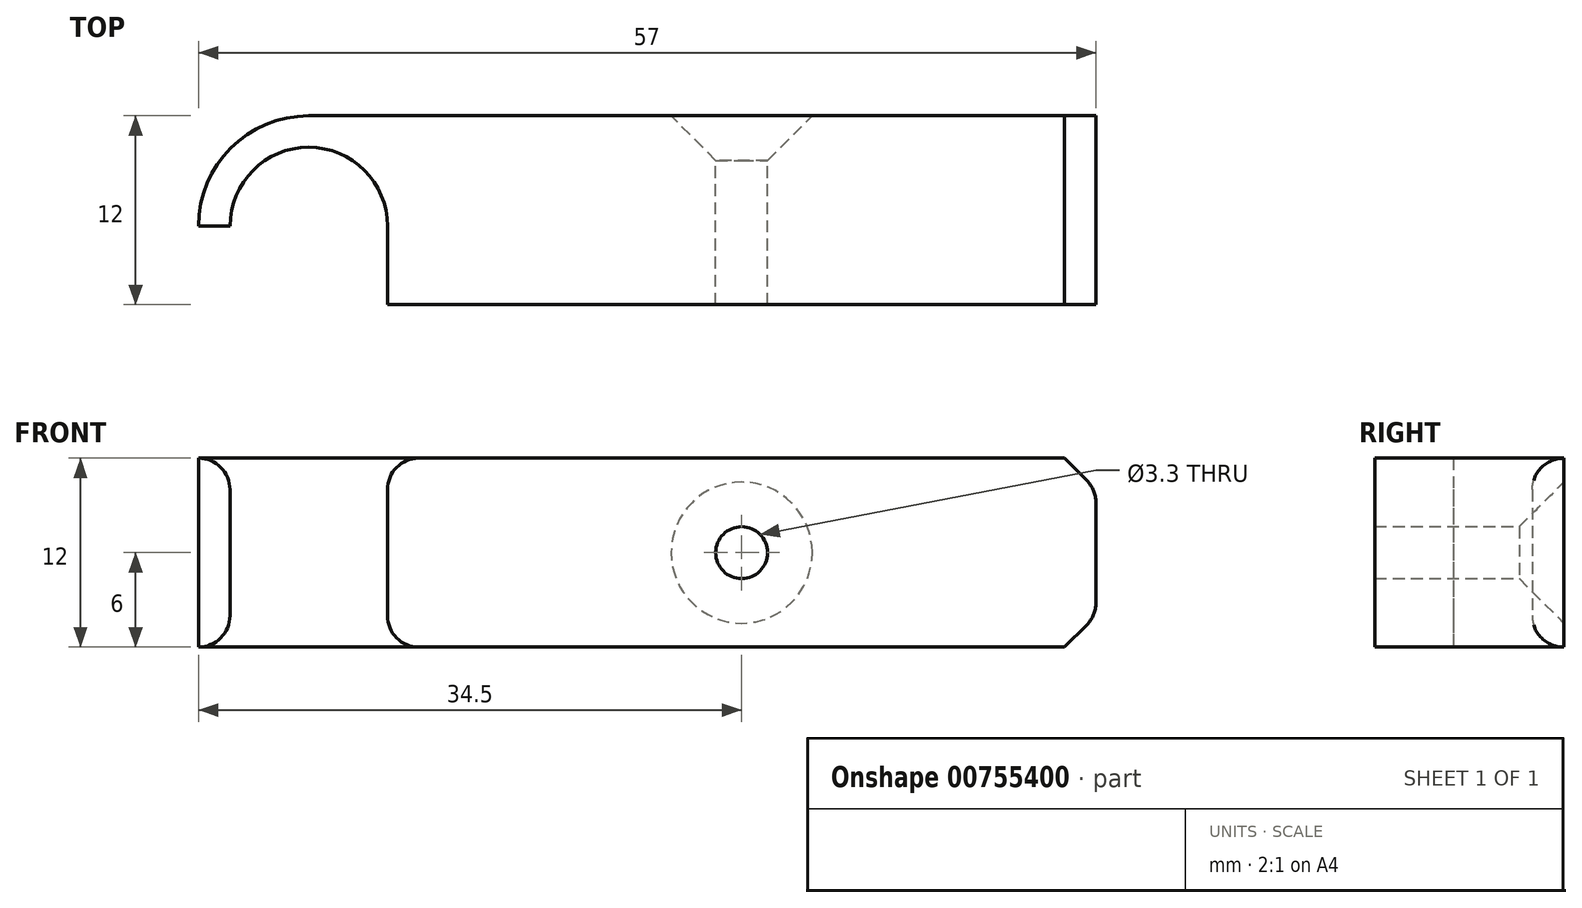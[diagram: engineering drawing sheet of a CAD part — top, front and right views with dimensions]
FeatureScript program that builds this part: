
annotation { "Feature Type Name" : "Feature", "Feature Type Description" : "" }
export const myFeature = defineFeature(function(context is Context, id is Id, definition is map)
    precondition{}
    {
        {
            var Q0;
            Q0=qCreatedBy(makeId("Top.planeOp"),FACE);
            var sketch = newSketch(context, id + "F0", { "sketchPlane" : qUnion([Q0])});
            skArc(sketch, "E0", {"start": v(5, 0) * mm, "mid": v(0, 5) * mm, "end": v(-5, 0) * mm});
            skArc(sketch, "E1.0", {"start": v(0, 7) * mm, "mid": v(-4.95, 4.95) * mm, "end": v(-7, 0) * mm});
            skLineSegment(sketch, "E2", {"start": v(0, 7) * mm, "end": v(50, 7) * mm});
            skLineSegment(sketch, "E3", {"start": v(50, 7) * mm, "end": v(50, -5) * mm});
            skLineSegment(sketch, "E4", {"start": v(50, -5) * mm, "end": v(5, -5) * mm});
            skLineSegment(sketch, "E5", {"start": v(-7, 0) * mm, "end": v(-5, 0) * mm});
            skLineSegment(sketch, "E6", {"start": v(5, 0) * mm, "end": v(5, -5) * mm});
            skPoint(sketch, "E7.orphan", {"position": v(0, -5) * mm});
            skSolve(sketch);
        }
        {
            var Q0;
            Q0=makeQuery(id+"F0.imprint","IMPRINT",FACE,{"disambiguationData":[TD([[makeQuery(id+"F0.imprint","IMPRINT",EDGE,{"derivedFrom":sQuery(id+"F0.wireOp",EDGE,"E0")}),-1.0]])]});
            extrude(context, id + "F1", {"entities" : qUnion([Q0]), "depth" : 12 * mm, "offsetDistance" : 25 * mm, "symmetric" : true});
        }
        {
            var Q0;
            Q0=makeQuery(id+"F1.opExtrude","SWEPT_FACE",FACE,{"disambiguationData":[OSD([sQuery(id+"F0.wireOp",EDGE,"E2")])]});
            var sketch = newSketch(context, id + "F2", { "sketchPlane" : qUnion([Q0])});
            skLineSegment(sketch, "E8", {"start": v(-50, 6) * mm, "end": v(-5, -6) * mm, "construction": true});
            skPoint(sketch, "E9", {"position": v(-27.5, 0) * mm});
            skSolve(sketch);
        }
        {
            var Q0;
            Q0=sQuery(id+"F2.wireOp",VERTEX,"E9");
            var Q1;
            Q1=makeQuery(id+"F1.opExtrude","SWEPT_BODY",BODY,{"disambiguationData":[OSD([sQuery(id+"F0.wireOp",EDGE,"E0"),sQuery(id+"F0.wireOp",EDGE,"E1.0"),sQuery(id+"F0.wireOp",EDGE,"E2"),sQuery(id+"F0.wireOp",EDGE,"E3"),sQuery(id+"F0.wireOp",EDGE,"E4"),sQuery(id+"F0.wireOp",EDGE,"E5"),sQuery(id+"F0.wireOp",EDGE,"E6")])]});
            hole(context, id + "F3", {"style" : HoleStyle.C_SINK, "endStyle" : HoleEndStyle.THROUGH, "standardTappedOrClearance" : lookupTablePath({ "standard" : "ISO", "engagement" : "75%", "pitch" : "0.7 mm", "size" : "M4", "type" : "Tapped" }), "standardBlindInLast" : lookupTablePath({ "standard" : "ISO", "engagement" : "75%", "pitch" : "0.7 mm", "size" : "M4", "type" : "Tapped" }), "holeDiameter" : 3.3 * mm, "cSinkDiameter" : 8.96 * mm, "cSinkAngle" : 90 * degree, "majorDiameter" : 4 * mm, "showTappedDepth" : true, "isTappedThrough" : true, "tappedDepth" : 12 * mm, "tapClearance" : 3, "locations" : qUnion([Q0]), "scope" : qUnion([Q1])});
        }
        {
            var Q0;
            Q0=makeQuery(id+"F1.opExtrude","CAP_EDGE",EDGE,{"disambiguationData":[OSD([sQuery(id+"F0.wireOp",EDGE,"E3")])],"isStart":false});
            var Q1;
            Q1=makeQuery(id+"F1.opExtrude","CAP_EDGE",EDGE,{"disambiguationData":[OSD([sQuery(id+"F0.wireOp",EDGE,"E3")])],"isStart":true});
            chamfer(context, id + "F4", {"entities" : qUnion([Q0, Q1]), "width" : 2 * mm, "tangentPropagation" : true});
        }
        {
            var Q0;
            {var subQ0=sQuery(id+"F0.wireOp",EDGE,"E3");Q0=makeQuery(id+"F4.opChamfer","BLEND_EDGE",EDGE,{"blendedFrom":[makeQuery(id+"F1.opExtrude","CAP_EDGE",EDGE,{"disambiguationData":[OSD([subQ0])],"isStart":false}),makeQuery(id+"F1.opExtrude","SWEPT_FACE",FACE,{"disambiguationData":[OSD([subQ0])]})],"blendedInto":[makeQuery(id+"F1.opExtrude","SWEPT_FACE",FACE,{"disambiguationData":[OSD([subQ0])]})]});}
            var Q1;
            {var subQ0=sQuery(id+"F0.wireOp",EDGE,"E3");Q1=makeQuery(id+"F4.opChamfer","BLEND_EDGE",EDGE,{"blendedFrom":[makeQuery(id+"F1.opExtrude","CAP_EDGE",EDGE,{"disambiguationData":[OSD([subQ0])],"isStart":true}),makeQuery(id+"F1.opExtrude","SWEPT_FACE",FACE,{"disambiguationData":[OSD([subQ0])]})],"blendedInto":[makeQuery(id+"F1.opExtrude","SWEPT_FACE",FACE,{"disambiguationData":[OSD([subQ0])]})]});}
            fillet(context, id + "F5", {"entities" : qUnion([Q0, Q1]), "radius" : 2 * mm, "tangentPropagation" : true, "allowEdgeOverflow" : false});
        }
        {
            var Q0;
            Q0=makeQuery(id+"F1.opExtrude","CAP_EDGE",EDGE,{"disambiguationData":[OSD([sQuery(id+"F0.wireOp",EDGE,"E0")])],"isStart":false});
            fillet(context, id + "F6", {"entities" : qUnion([Q0]), "radius" : 2 * mm, "tangentPropagation" : true, "allowEdgeOverflow" : false});
        }
        {
            var Q0;
            Q0=makeQuery(id+"F1.opExtrude","CAP_EDGE",EDGE,{"disambiguationData":[OSD([sQuery(id+"F0.wireOp",EDGE,"E0")])],"isStart":true});
            fillet(context, id + "F7", {"entities" : qUnion([Q0]), "radius" : 2 * mm, "tangentPropagation" : true, "allowEdgeOverflow" : false});
        }
    });
